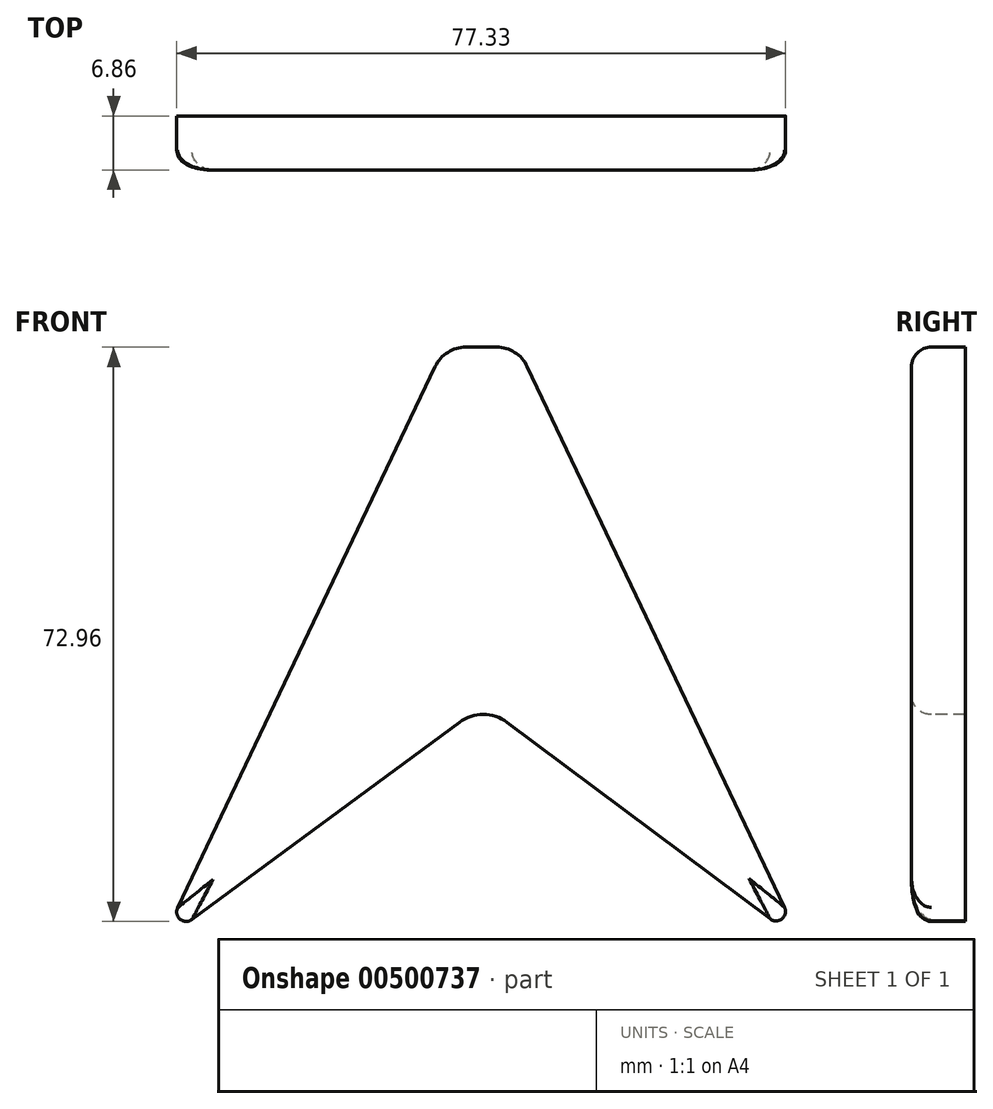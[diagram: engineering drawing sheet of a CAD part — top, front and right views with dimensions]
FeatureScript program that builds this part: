
annotation { "Feature Type Name" : "Feature", "Feature Type Description" : "" }
export const myFeature = defineFeature(function(context is Context, id is Id, definition is map)
    precondition{}
    {
        {
            var Q0;
            Q0=qCreatedBy(makeId("Front.planeOp"),FACE);
            var sketch = newSketch(context, id + "F0", { "sketchPlane" : qUnion([Q0])});
            skLineSegment(sketch, "E0", {"start": v(0, 43.39) * mm, "end": v(-9.34, 43.39) * mm});
            skLineSegment(sketch, "E1", {"start": v(-9.34, 43.39) * mm, "end": v(-45.31, -32.2) * mm});
            skLineSegment(sketch, "E2", {"start": v(0, 43.39) * mm, "end": v(35.97, -32.2) * mm});
            skLineSegment(sketch, "E3", {"start": v(-45.31, -32.2) * mm, "end": v(-4.4, -2.03) * mm});
            skLineSegment(sketch, "E4", {"start": v(-4.4, -2.03) * mm, "end": v(35.97, -32.2) * mm});
            skSolve(sketch);
        }
        {
            var Q0;
            Q0=makeQuery(id+"F0.imprint","IMPRINT",FACE,{"disambiguationData":[TD([[makeQuery(id+"F0.imprint","IMPRINT",EDGE,{"derivedFrom":sQuery(id+"F0.wireOp",EDGE,"E0")}),1.0]])]});
            extrude(context, id + "F1", {"entities" : qUnion([Q0]), "depth" : 6.86 * mm});
        }
        {
            var Q0;
            Q0=makeQuery(id+"F1.opExtrude","SWEPT_EDGE",EDGE,{"disambiguationData":[OSD([sQuery(id+"F0.wireOp",EDGE,"E1"),sQuery(id+"F0.wireOp",EDGE,"E3")])]});
            var Q1;
            Q1=makeQuery(id+"F1.opExtrude","SWEPT_EDGE",EDGE,{"disambiguationData":[OSD([sQuery(id+"F0.wireOp",EDGE,"E2"),sQuery(id+"F0.wireOp",EDGE,"E4")])]});
            fillet(context, id + "F2", {"entities" : qUnion([Q0, Q1]), "radius" : 1.21 * mm, "tangentPropagation" : true, "allowEdgeOverflow" : false});
        }
        {
            var Q0;
            Q0=makeQuery(id+"F1.opExtrude","SWEPT_EDGE",EDGE,{"disambiguationData":[OSD([sQuery(id+"F0.wireOp",EDGE,"E3"),sQuery(id+"F0.wireOp",EDGE,"E4")])]});
            fillet(context, id + "F3", {"entities" : qUnion([Q0]), "radius" : 5.08 * mm, "tangentPropagation" : true, "allowEdgeOverflow" : false});
        }
        {
            var Q0;
            Q0=makeQuery(id+"F1.opExtrude","SWEPT_EDGE",EDGE,{"disambiguationData":[OSD([sQuery(id+"F0.wireOp",EDGE,"E0"),sQuery(id+"F0.wireOp",EDGE,"E1")])]});
            var Q1;
            Q1=makeQuery(id+"F1.opExtrude","SWEPT_EDGE",EDGE,{"disambiguationData":[OSD([sQuery(id+"F0.wireOp",EDGE,"E0"),sQuery(id+"F0.wireOp",EDGE,"E2")])]});
            fillet(context, id + "F4", {"entities" : qUnion([Q0, Q1]), "radius" : 4.3 * mm, "tangentPropagation" : true, "allowEdgeOverflow" : false});
        }
        {
            var Q0;
            Q0=makeQuery(id+"F1.opExtrude","CAP_EDGE",EDGE,{"disambiguationData":[OSD([sQuery(id+"F0.wireOp",EDGE,"E2")])],"isStart":false});
            fillet(context, id + "F5", {"entities" : qUnion([Q0]), "radius" : 2.5 * mm, "tangentPropagation" : true, "allowEdgeOverflow" : false});
        }
    });
